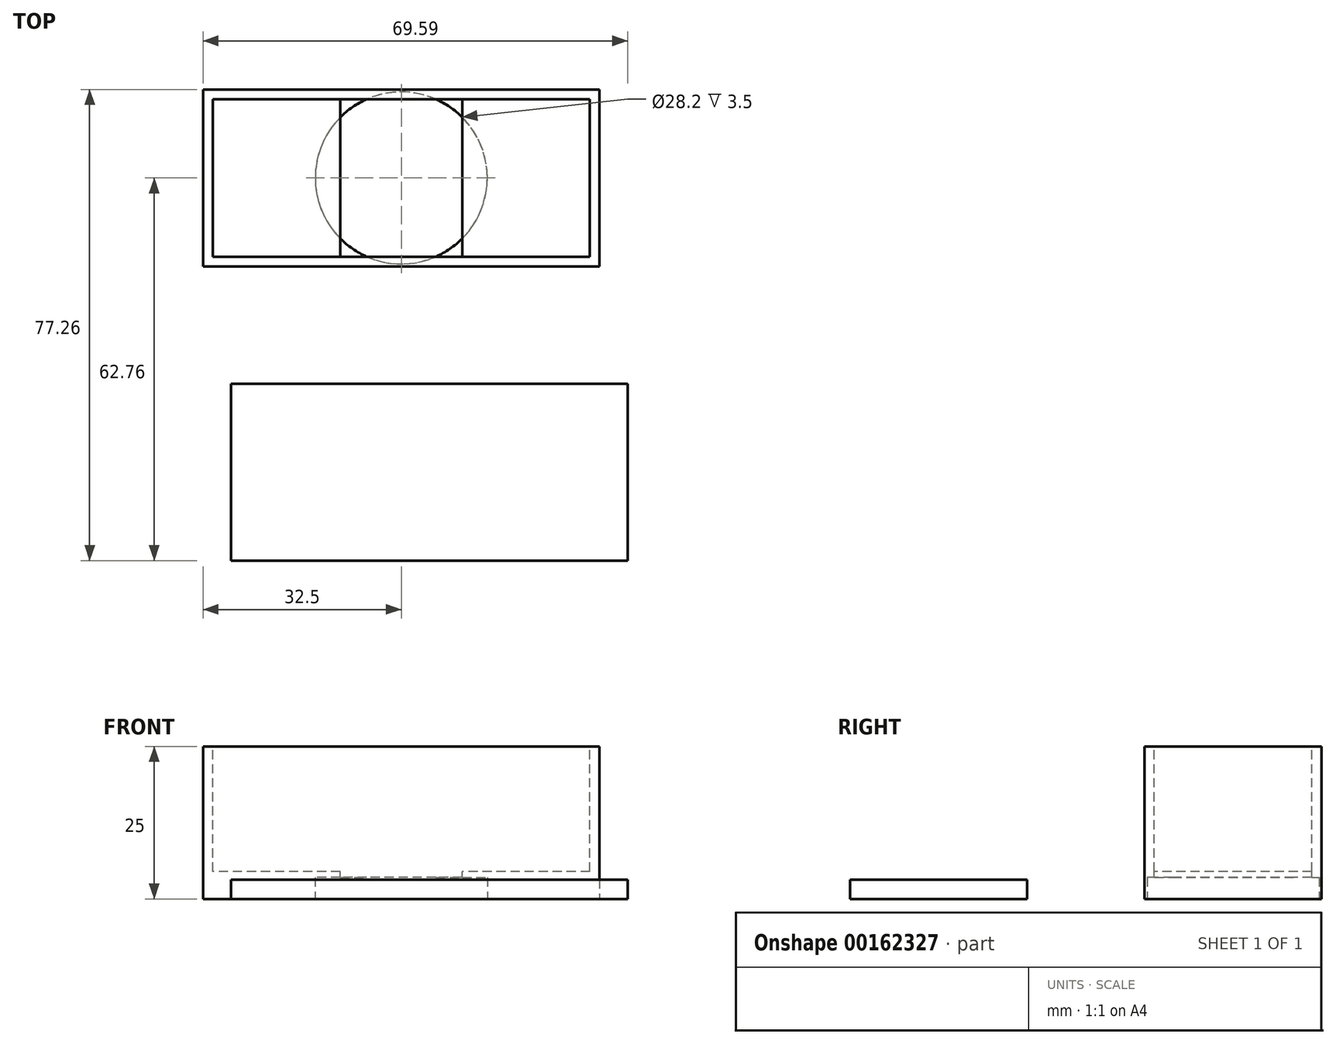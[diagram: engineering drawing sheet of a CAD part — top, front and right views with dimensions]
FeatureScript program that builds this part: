
annotation { "Feature Type Name" : "Feature", "Feature Type Description" : "" }
export const myFeature = defineFeature(function(context is Context, id is Id, definition is map)
    precondition{}
    {
        {
            var Q0;
            Q0=qCreatedBy(makeId("Top.planeOp"),FACE);
            var sketch = newSketch(context, id + "F0", { "sketchPlane" : qUnion([Q0])});
            skLineSegment(sketch, "E0.bottom", {"start": v(-32.5, -14.5) * mm, "end": v(32.5, -14.5) * mm});
            skLineSegment(sketch, "E0.top", {"start": v(-32.5, 14.5) * mm, "end": v(32.5, 14.5) * mm});
            skLineSegment(sketch, "E0.left", {"start": v(-32.5, -14.5) * mm, "end": v(-32.5, 14.5) * mm});
            skLineSegment(sketch, "E0.right", {"start": v(32.5, -14.5) * mm, "end": v(32.5, 14.5) * mm});
            skPoint(sketch, "E1", {"position": v(0, 14.5) * mm});
            skPoint(sketch, "E2", {"position": v(-32.5, 0) * mm});
            skSolve(sketch);
        }
        {
            var Q0;
            Q0=makeQuery(id+"F0.imprint","IMPRINT",FACE,{"disambiguationData":[TD([[makeQuery(id+"F0.imprint","IMPRINT",EDGE,{"derivedFrom":sQuery(id+"F0.wireOp",EDGE,"E0.bottom")}),1.0]])]});
            extrude(context, id + "F1", {"entities" : qUnion([Q0]), "depth" : 25 * mm});
        }
        {
            var Q0;
            Q0=qCreatedBy(makeId("Top.planeOp"),FACE);
            var sketch = newSketch(context, id + "F2", { "sketchPlane" : qUnion([Q0])});
            skCircle(sketch, "E3", {"center": v(0, 0) * mm, "radius": 14.1 * mm});
            skSolve(sketch);
        }
        {
            var Q0;
            Q0=makeQuery(id+"F2.imprint","IMPRINT",FACE,{"disambiguationData":[TD([[makeQuery(id+"F2.imprint","IMPRINT",EDGE,{"derivedFrom":sQuery(id+"F2.wireOp",EDGE,"E3")}),1.0]])]});
            extrude(context, id + "F3", {"entities" : qUnion([Q0]), "operationType" : NewBodyOperationType.REMOVE, "depth" : 3.5 * mm});
        }
        {
            var Q0;
            Q0=makeQuery(id+"F1.opExtrude","CAP_FACE",FACE,{"disambiguationData":[OSD([sQuery(id+"F0.wireOp",EDGE,"E0.bottom"),sQuery(id+"F0.wireOp",EDGE,"E0.top"),sQuery(id+"F0.wireOp",EDGE,"E0.left"),sQuery(id+"F0.wireOp",EDGE,"E0.right")])],"isStart":false});
            var sketch = newSketch(context, id + "F4", { "sketchPlane" : qUnion([Q0])});
            skLineSegment(sketch, "E4.0", {"start": v(-30.91, 12.91) * mm, "end": v(-30.91, -12.91) * mm});
            skLineSegment(sketch, "E4.1", {"start": v(30.91, 12.91) * mm, "end": v(-30.91, 12.91) * mm});
            skLineSegment(sketch, "E4.2", {"start": v(30.91, -12.91) * mm, "end": v(30.91, 12.91) * mm});
            skLineSegment(sketch, "E4.3", {"start": v(-30.91, -12.91) * mm, "end": v(30.91, -12.91) * mm});
            skSolve(sketch);
        }
        {
            var Q0;
            Q0=makeQuery(id+"F4.imprint","IMPRINT",FACE,{"disambiguationData":[TD([[makeQuery(id+"F4.imprint","IMPRINT",EDGE,{"derivedFrom":sQuery(id+"F4.wireOp",EDGE,"E4.0")}),1.0]])]});
            extrude(context, id + "F5", {"entities" : qUnion([Q0]), "operationType" : NewBodyOperationType.REMOVE, "oppositeDirection" : true, "depth" : 20.5 * mm});
        }
        {
            var Q0;
            Q0=qCreatedBy(makeId("Top.planeOp"),FACE);
            var sketch = newSketch(context, id + "F6", { "sketchPlane" : qUnion([Q0])});
            skLineSegment(sketch, "E5.bottom", {"start": v(-27.9, -62.76) * mm, "end": v(37.1, -62.76) * mm});
            skLineSegment(sketch, "E5.top", {"start": v(-27.9, -33.76) * mm, "end": v(37.1, -33.76) * mm});
            skLineSegment(sketch, "E5.left", {"start": v(-27.9, -62.76) * mm, "end": v(-27.9, -33.76) * mm});
            skLineSegment(sketch, "E5.right", {"start": v(37.1, -62.76) * mm, "end": v(37.1, -33.76) * mm});
            skSolve(sketch);
        }
        {
            var Q0;
            Q0=makeQuery(id+"F6.imprint","IMPRINT",FACE,{"disambiguationData":[TD([[makeQuery(id+"F6.imprint","IMPRINT",EDGE,{"derivedFrom":sQuery(id+"F6.wireOp",EDGE,"E5.bottom")}),1.0]])]});
            extrude(context, id + "F7", {"entities" : qUnion([Q0]), "depth" : 3.17 * mm});
        }
        {
            var Q0;
            Q0=makeQuery(id+"F5.boolean.opBoolean","COPY",FACE,{"derivedFrom":makeQuery(id+"F5.opExtrude","CAP_FACE",FACE,{"disambiguationData":[OSD([sQuery(id+"F4.wireOp",EDGE,"E4.0"),sQuery(id+"F4.wireOp",EDGE,"E4.1"),sQuery(id+"F4.wireOp",EDGE,"E4.2"),sQuery(id+"F4.wireOp",EDGE,"E4.3")])],"isStart":false})});
            var sketch = newSketch(context, id + "F8", { "sketchPlane" : qUnion([Q0])});
            skLineSegment(sketch, "E6.bottom", {"start": v(-10, 12.91) * mm, "end": v(10, 12.91) * mm});
            skLineSegment(sketch, "E6.top", {"start": v(-10, -12.91) * mm, "end": v(10, -12.91) * mm});
            skLineSegment(sketch, "E6.left", {"start": v(-10, 12.91) * mm, "end": v(-10, -12.91) * mm});
            skLineSegment(sketch, "E6.right", {"start": v(10, 12.91) * mm, "end": v(10, -12.91) * mm});
            skSolve(sketch);
        }
        {
            var Q0;
            Q0=makeQuery(id+"F8.imprint","IMPRINT",FACE,{"disambiguationData":[TD([[makeQuery(id+"F8.imprint","IMPRINT",EDGE,{"derivedFrom":sQuery(id+"F8.wireOp",EDGE,"E6.bottom")}),1.0]])]});
            extrude(context, id + "F9", {"entities" : qUnion([Q0]), "operationType" : NewBodyOperationType.REMOVE, "oppositeDirection" : true, "depth" : 1 * mm});
        }
    });
